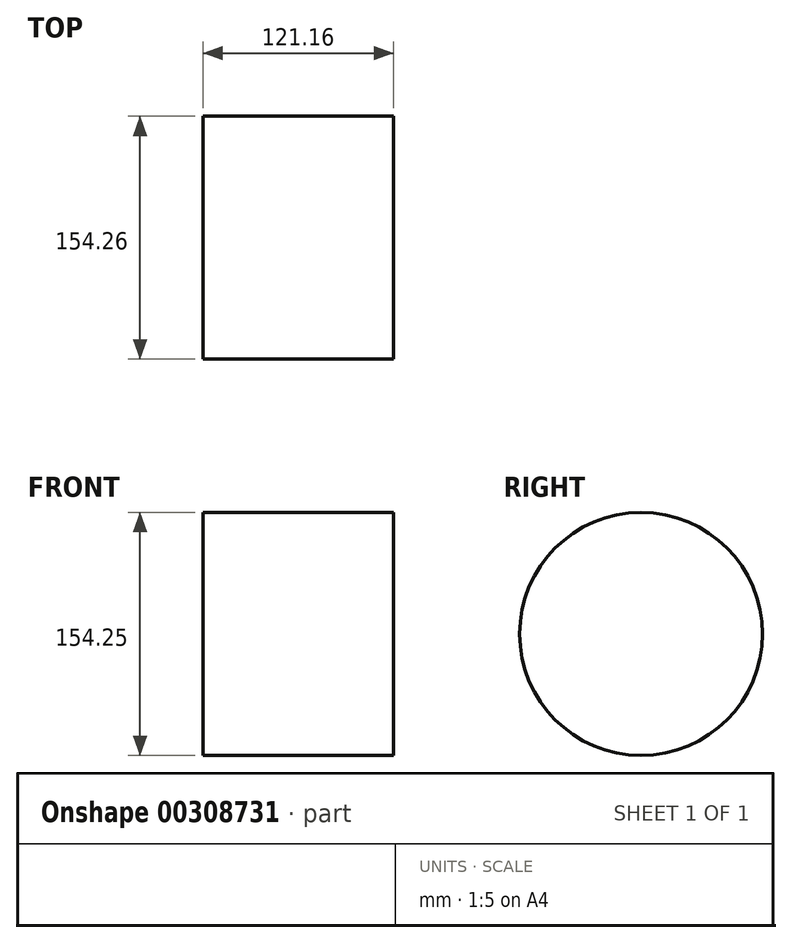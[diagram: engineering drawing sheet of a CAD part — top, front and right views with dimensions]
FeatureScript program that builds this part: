
annotation { "Feature Type Name" : "Feature", "Feature Type Description" : "" }
export const myFeature = defineFeature(function(context is Context, id is Id, definition is map)
    precondition{}
    {
        {
            var Q0;
            Q0=qCreatedBy(makeId("Right.planeOp"),FACE);
            var sketch = newSketch(context, id + "F0", { "sketchPlane" : qUnion([Q0])});
            skCircle(sketch, "E0", {"center": v(-30.44, 27.77) * mm, "radius": 77.13 * mm});
            skSolve(sketch);
        }
        {
            var Q0;
            Q0=makeQuery(id+"F0.imprint","IMPRINT",FACE,{"disambiguationData":[TD([[makeQuery(id+"F0.imprint","IMPRINT",EDGE,{"derivedFrom":sQuery(id+"F0.wireOp",EDGE,"E0")}),1.0]])]});
            extrude(context, id + "F1", {"entities" : qUnion([Q0]), "depth" : 121.16 * mm});
        }
    });
